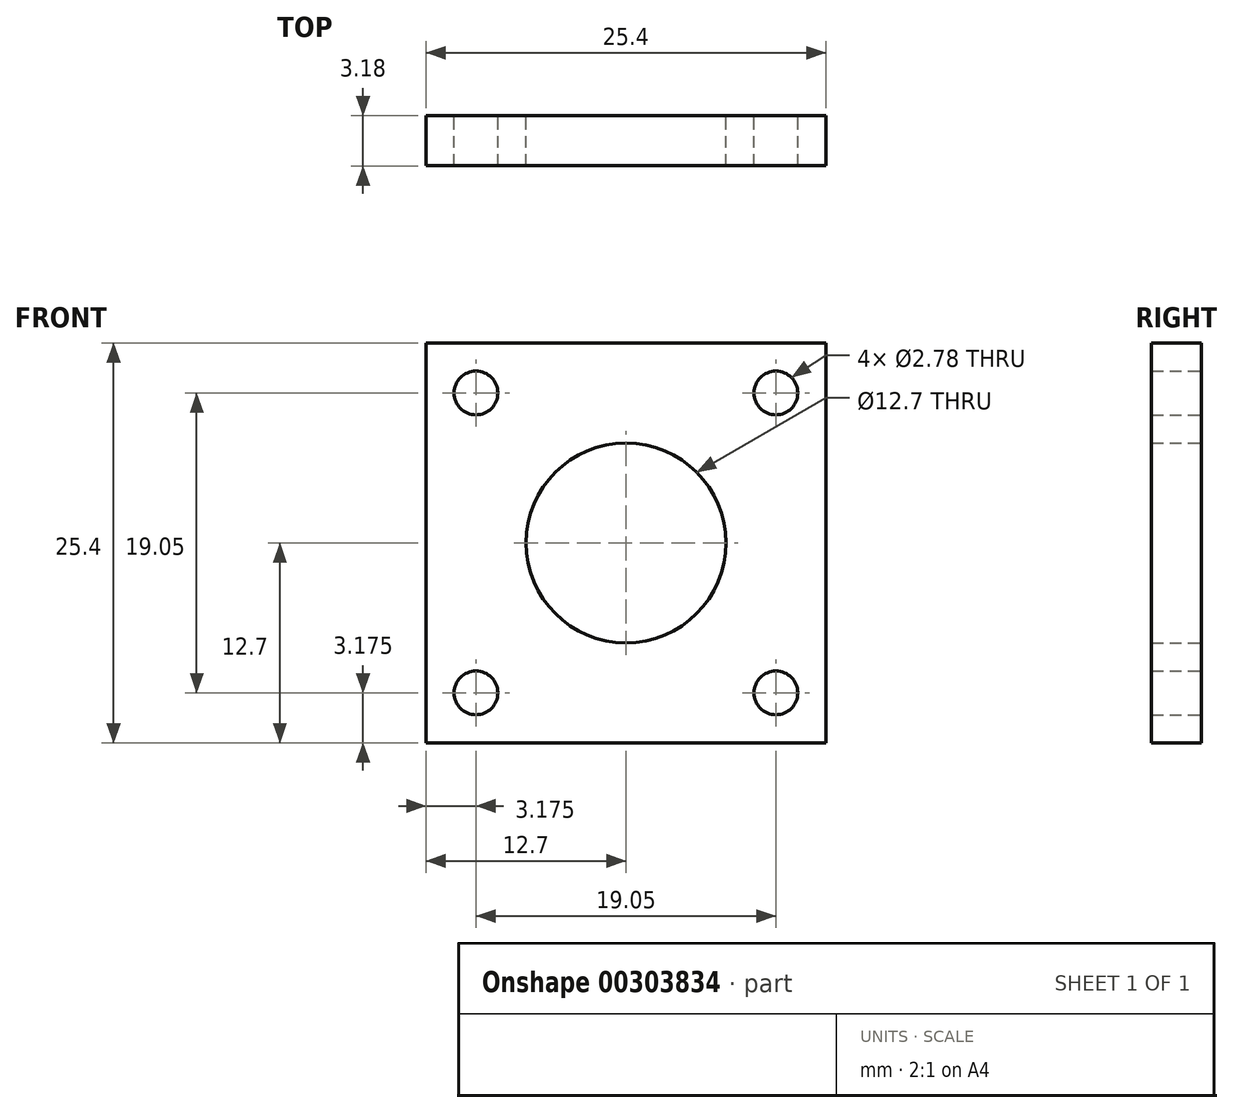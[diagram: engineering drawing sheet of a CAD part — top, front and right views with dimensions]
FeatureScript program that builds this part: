
annotation { "Feature Type Name" : "Feature", "Feature Type Description" : "" }
export const myFeature = defineFeature(function(context is Context, id is Id, definition is map)
    precondition{}
    {
        {
            var Q0;
            Q0=qCreatedBy(makeId("Front.planeOp"),FACE);
            var sketch = newSketch(context, id + "F0", { "sketchPlane" : qUnion([Q0])});
            skLineSegment(sketch, "E0.bottom", {"start": v(0, 0) * mm, "end": v(-25.4, 0) * mm});
            skLineSegment(sketch, "E0.top", {"start": v(0, -25.4) * mm, "end": v(-25.4, -25.4) * mm});
            skLineSegment(sketch, "E0.left", {"start": v(0, 0) * mm, "end": v(0, -25.4) * mm});
            skLineSegment(sketch, "E0.right", {"start": v(-25.4, 0) * mm, "end": v(-25.4, -25.4) * mm});
            skCircle(sketch, "E1", {"center": v(-12.7, -12.7) * mm, "radius": 6.35 * mm});
            skLineSegment(sketch, "E2.bottom", {"start": v(-25.4, 0) * mm, "end": v(-22.22, 0) * mm});
            skLineSegment(sketch, "E2.left", {"start": v(-25.4, 0) * mm, "end": v(-25.4, -3.17) * mm});
            skCircle(sketch, "E3", {"center": v(-22.22, -3.17) * mm, "radius": 1.39 * mm});
            skLineSegment(sketch, "E4.bottom", {"start": v(0, 0) * mm, "end": v(-3.17, 0) * mm});
            skLineSegment(sketch, "E4.left", {"start": v(0, 0) * mm, "end": v(0, -3.17) * mm});
            skCircle(sketch, "E5", {"center": v(-3.17, -3.18) * mm, "radius": 1.39 * mm});
            skLineSegment(sketch, "E6.bottom", {"start": v(-25.4, -25.4) * mm, "end": v(-22.22, -25.4) * mm});
            skLineSegment(sketch, "E6.left", {"start": v(-25.4, -25.4) * mm, "end": v(-25.4, -22.22) * mm});
            skLineSegment(sketch, "E7.bottom", {"start": v(0, -25.4) * mm, "end": v(-3.17, -25.4) * mm});
            skLineSegment(sketch, "E7.left", {"start": v(0, -25.4) * mm, "end": v(0, -22.22) * mm});
            skCircle(sketch, "E8", {"center": v(-22.22, -22.22) * mm, "radius": 1.39 * mm});
            skCircle(sketch, "E9", {"center": v(-3.17, -22.22) * mm, "radius": 1.39 * mm});
            skSolve(sketch);
        }
        {
            var Q0;
            Q0=makeQuery(id+"F0.imprint","IMPRINT",FACE,{"disambiguationData":[TD([[makeQuery(id+"F0.imprint","IMPRINT",EDGE,{"derivedFrom":sQuery(id+"F0.wireOp",EDGE,"E0.bottom")}),1.0]])]});
            extrude(context, id + "F1", {"entities" : qUnion([Q0]), "depth" : 3.17 * mm});
        }
    });
